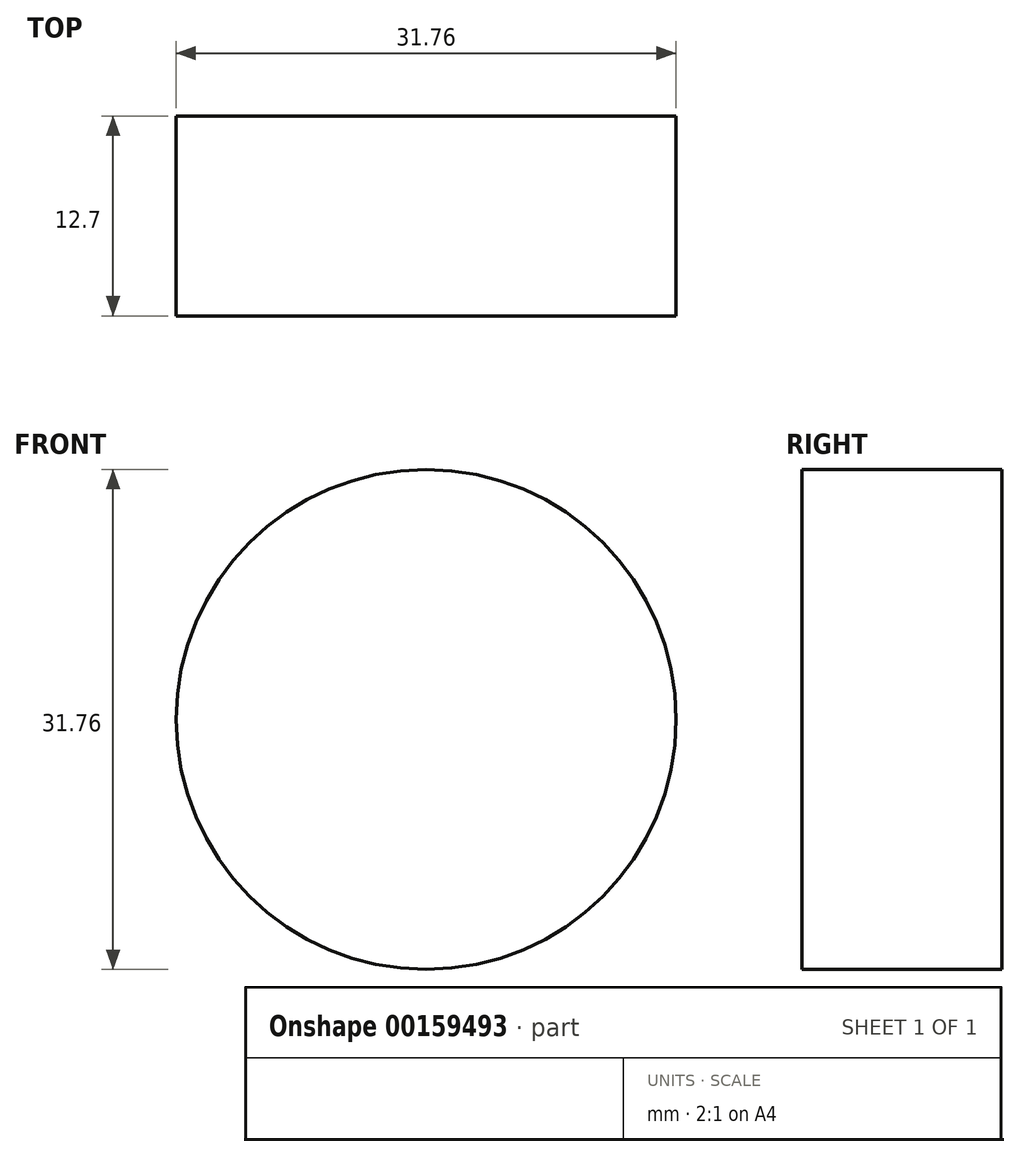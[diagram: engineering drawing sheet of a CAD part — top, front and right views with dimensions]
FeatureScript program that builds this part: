
annotation { "Feature Type Name" : "Feature", "Feature Type Description" : "" }
export const myFeature = defineFeature(function(context is Context, id is Id, definition is map)
    precondition{}
    {
        {
            var Q0;
            Q0=qCreatedBy(makeId("Front.planeOp"),FACE);
            var sketch = newSketch(context, id + "F0", { "sketchPlane" : qUnion([Q0])});
            skCircle(sketch, "E0", {"center": v(0, 0) * mm, "radius": 15.88 * mm});
            skSolve(sketch);
        }
        {
            var Q0;
            Q0 = qSketchRegion(id + "F0", true);
            extrude(context, id + "F1", {"entities" : qUnion([Q0]), "depth" : 12.7 * mm});
        }
    });
